# Revit family: Odyssey Surface Mount
name_source: partatom
category: Lighting Fixtures
revit_build: Autodesk Revit 2017 (Build: 20190508_0315(x64)
units: mm (PartAtom-declared; Revit-internal decimal feet)

## family parameters
Cut with Voids When Loaded = No
Host = Face
Light Source = Yes
Part Type = Normal
Room Calculation Point = No
Round Connector Dimension = Use Diameter
Shared = No

## types (1)
- Odyssey Surface Mount
    Canopy Width = 5"
    Color Filter = 16777215
    Cost = 279 $
    Default Elevation = 0"
    Description = An elemental take on track lighting, the Odyssey family marries sophistication and adjustability. Suspended from a minimalist canopy, the opposing arms terminate in a swiveling socket cup, allowing for some play with light placement. This bare bulb surface mount is a real shiner when grouped in multiples extending the length of corridors or accentuating linear counter tops and furniture groupings. Personalize with your choice of bulb and update according to mood or season for dramatically different looks. Assembled in our Portland, Ore. factory using ethically-sourced domestic and global components. A Schoolhouse Original.
    Dimming Lamp Color Temperature Shift = <None>
    Height = 6"
    Length = 6"
    Light Source Symbol Size = 2"
    Max Wattage = 60 W
    Primary Finishes = True Black, Natural Brass
    Product Material = Steel
    URL = https://www.schoolhouse.com
    Voltage = 120 /220V
    Width = 22"

## geometry (parser evidence)
native form markers: Sweep x4
no freeform markers — native parametric forms only
